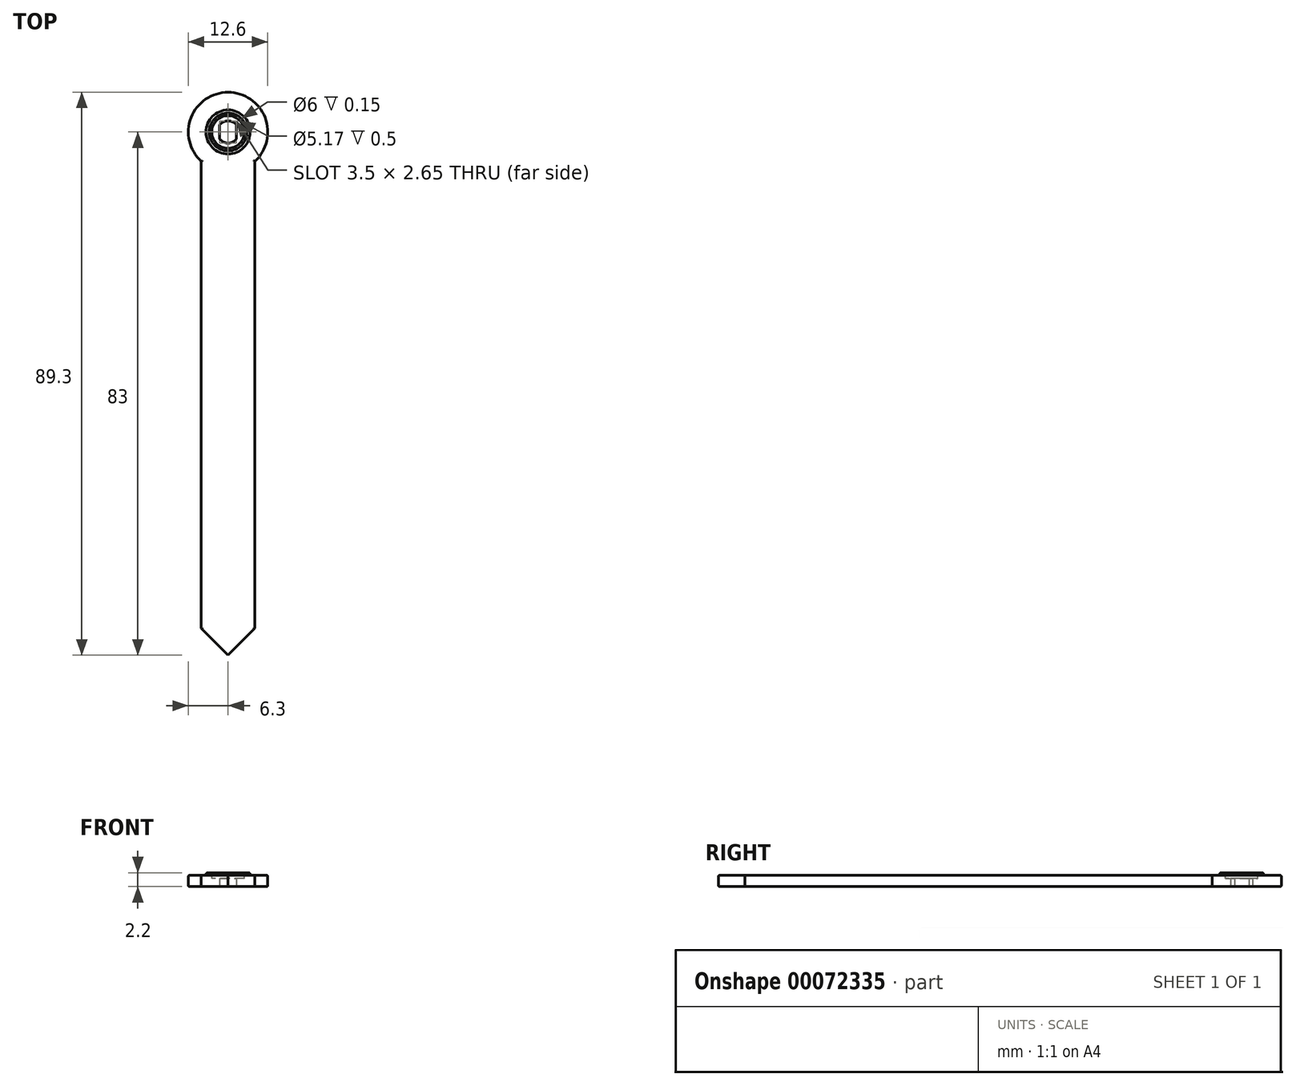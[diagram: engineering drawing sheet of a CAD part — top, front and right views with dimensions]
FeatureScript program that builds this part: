
annotation { "Feature Type Name" : "Feature", "Feature Type Description" : "" }
export const myFeature = defineFeature(function(context is Context, id is Id, definition is map)
    precondition{}
    {
        {
            var Q0;
            Q0=qCreatedBy(makeId("Top.planeOp"),FACE);
            var sketch = newSketch(context, id + "F0", { "sketchPlane" : qUnion([Q0])});
            skArc(sketch, "E0", {"start": v(4.25, -4.65) * mm, "mid": v(0, 6.3) * mm, "end": v(-4.25, -4.65) * mm});
            skArc(sketch, "E1", {"start": v(-1.32, -1.14) * mm, "mid": v(0, -1.75) * mm, "end": v(1.33, -1.14) * mm});
            skLineSegment(sketch, "E2", {"start": v(-1.32, 1.14) * mm, "end": v(-1.32, -1.14) * mm});
            skLineSegment(sketch, "E3", {"start": v(1.33, 1.14) * mm, "end": v(1.33, -1.14) * mm});
            skPoint(sketch, "E4.orphan", {"position": v(-1.32, 2.66) * mm});
            skPoint(sketch, "E5.orphan", {"position": v(1.32, 2.92) * mm});
            skArc(sketch, "E6.trimOffspring", {"start": v(1.32, 1.14) * mm, "mid": v(0, 1.75) * mm, "end": v(-1.32, 1.14) * mm});
            skCircle(sketch, "E7", {"center": v(0, 0) * mm, "radius": 3 * mm});
            skCircle(sketch, "E8", {"center": v(0, 0) * mm, "radius": 3.5 * mm});
            skLineSegment(sketch, "E9", {"start": v(-4.25, -4.65) * mm, "end": v(-4.25, -78.75) * mm});
            skLineSegment(sketch, "E10", {"start": v(-4.25, -78.75) * mm, "end": v(0, -83) * mm});
            skLineSegment(sketch, "E11.MirrorCS", {"start": v(4.25, -4.65) * mm, "end": v(4.25, -78.75) * mm});
            skLineSegment(sketch, "E12.MirrorCS", {"start": v(4.25, -78.75) * mm, "end": v(0, -83) * mm});
            skSolve(sketch);
        }
        {
            var Q0;
            Q0=makeQuery(id+"F0.imprint","IMPRINT",FACE,{"disambiguationData":[TD([[makeQuery(id+"F0.imprint","IMPRINT",EDGE,{"derivedFrom":sQuery(id+"F0.wireOp",EDGE,"E0")}),1.0]])]});
            var Q1;
            Q1=makeQuery(id+"F0.imprint","IMPRINT",FACE,{"disambiguationData":[TD([[makeQuery(id+"F0.imprint","IMPRINT",EDGE,{"derivedFrom":sQuery(id+"F0.wireOp",EDGE,"E1")}),-1.0]])]});
            var Q2;
            Q2=makeQuery(id+"F0.imprint","IMPRINT",FACE,{"disambiguationData":[TD([[makeQuery(id+"F0.imprint","IMPRINT",EDGE,{"derivedFrom":sQuery(id+"F0.wireOp",EDGE,"E7")}),-1.0]])]});
            extrude(context, id + "F1", {"entities" : qUnion([Q0, Q1, Q2]), "depth" : 1.8 * mm});
        }
        {
            var Q0;
            Q0=makeQuery(id+"F0.imprint","IMPRINT",FACE,{"disambiguationData":[TD([[makeQuery(id+"F0.imprint","IMPRINT",EDGE,{"derivedFrom":sQuery(id+"F0.wireOp",EDGE,"E7")}),-1.0]])]});
            extrude(context, id + "F2", {"entities" : qUnion([Q0]), "operationType" : NewBodyOperationType.ADD, "depth" : 2.2 * mm});
        }
        {
            var Q0;
            Q0=makeQuery(id+"F1.opExtrude","CAP_EDGE",EDGE,{"disambiguationData":[OSD([sQuery(id+"F0.wireOp",EDGE,"E9")])],"isStart":false});
            var Q1;
            Q1=makeQuery(id+"F1.opExtrude","CAP_EDGE",EDGE,{"disambiguationData":[OSD([sQuery(id+"F0.wireOp",EDGE,"E0")])],"isStart":false});
            var Q2;
            Q2=makeQuery(id+"F1.opExtrude","CAP_EDGE",EDGE,{"disambiguationData":[OSD([sQuery(id+"F0.wireOp",EDGE,"E11.MirrorCS")])],"isStart":false});
            var Q3;
            Q3=makeQuery(id+"F1.opExtrude","CAP_EDGE",EDGE,{"disambiguationData":[OSD([sQuery(id+"F0.wireOp",EDGE,"E12.MirrorCS")])],"isStart":false});
            var Q4;
            Q4=makeQuery(id+"F1.opExtrude","CAP_EDGE",EDGE,{"disambiguationData":[OSD([sQuery(id+"F0.wireOp",EDGE,"E10")])],"isStart":false});
            var Q5;
            Q5=makeQuery(id+"F1.opExtrude","CAP_EDGE",EDGE,{"disambiguationData":[OSD([sQuery(id+"F0.wireOp",EDGE,"E0")])],"isStart":true});
            var Q6;
            Q6=makeQuery(id+"F1.opExtrude","CAP_EDGE",EDGE,{"disambiguationData":[OSD([sQuery(id+"F0.wireOp",EDGE,"E11.MirrorCS")])],"isStart":true});
            var Q7;
            Q7=makeQuery(id+"F1.opExtrude","CAP_EDGE",EDGE,{"disambiguationData":[OSD([sQuery(id+"F0.wireOp",EDGE,"E9")])],"isStart":true});
            var Q8;
            Q8=makeQuery(id+"F1.opExtrude","CAP_EDGE",EDGE,{"disambiguationData":[OSD([sQuery(id+"F0.wireOp",EDGE,"E10")])],"isStart":true});
            var Q9;
            Q9=makeQuery(id+"F1.opExtrude","CAP_EDGE",EDGE,{"disambiguationData":[OSD([sQuery(id+"F0.wireOp",EDGE,"E12.MirrorCS")])],"isStart":true});
            fillet(context, id + "F3", {"entities" : qUnion([Q0, Q1, Q2, Q3, Q4, Q5, Q6, Q7, Q8, Q9]), "radius" : .2 * mm, "tangentPropagation" : true, "allowEdgeOverflow" : false});
        }
        {
            var Q0;
            Q0=makeQuery(id+"F2.opExtrude","CAP_EDGE",EDGE,{"disambiguationData":[OSD([sQuery(id+"F0.wireOp",EDGE,"E8")])],"isStart":false});
            var Q1;
            Q1=makeQuery(id+"F2.opExtrude","CAP_EDGE",EDGE,{"disambiguationData":[OSD([sQuery(id+"F0.wireOp",EDGE,"E7")])],"isStart":false});
            fillet(context, id + "F4", {"entities" : qUnion([Q0, Q1]), "radius" : .25 * mm, "tangentPropagation" : true, "allowEdgeOverflow" : false});
        }
        {
            var Q0;
            {var subQ0=sQuery(id+"F0.wireOp",EDGE,"E6.trimOffspring");var subQ1=sQuery(id+"F0.wireOp",EDGE,"E3");var subQ2=sQuery(id+"F0.wireOp",EDGE,"E2");var subQ3=sQuery(id+"F0.wireOp",EDGE,"E1");Q0=makeQuery(id+"F2.boolean.opBoolean","SPLIT",FACE,{"disambiguationData":[TD([makeQuery(id+"F1.opExtrude","SWEPT_FACE",FACE,{"disambiguationData":[OSD([subQ3])]})])],"derivedFrom":makeQuery(id+"F1.opExtrude","CAP_FACE",FACE,{"disambiguationData":[OSD([sQuery(id+"F0.wireOp",EDGE,"E0"),subQ3,subQ2,subQ1,subQ0,sQuery(id+"F0.wireOp",EDGE,"E9"),sQuery(id+"F0.wireOp",EDGE,"E10"),sQuery(id+"F0.wireOp",EDGE,"E11.MirrorCS"),sQuery(id+"F0.wireOp",EDGE,"E12.MirrorCS")])],"isStart":false})});}
            var sketch = newSketch(context, id + "F5", { "sketchPlane" : qUnion([Q0])});
            skCircle(sketch, "E13", {"center": v(0, 0) * mm, "radius": 2.59 * mm});
            skSolve(sketch);
        }
        {
            var Q0;
            Q0 = qSketchRegion(id + "F5", true);
            extrude(context, id + "F6", {"entities" : qUnion([Q0]), "operationType" : NewBodyOperationType.REMOVE, "oppositeDirection" : true, "depth" : .5 * mm});
        }
    });
